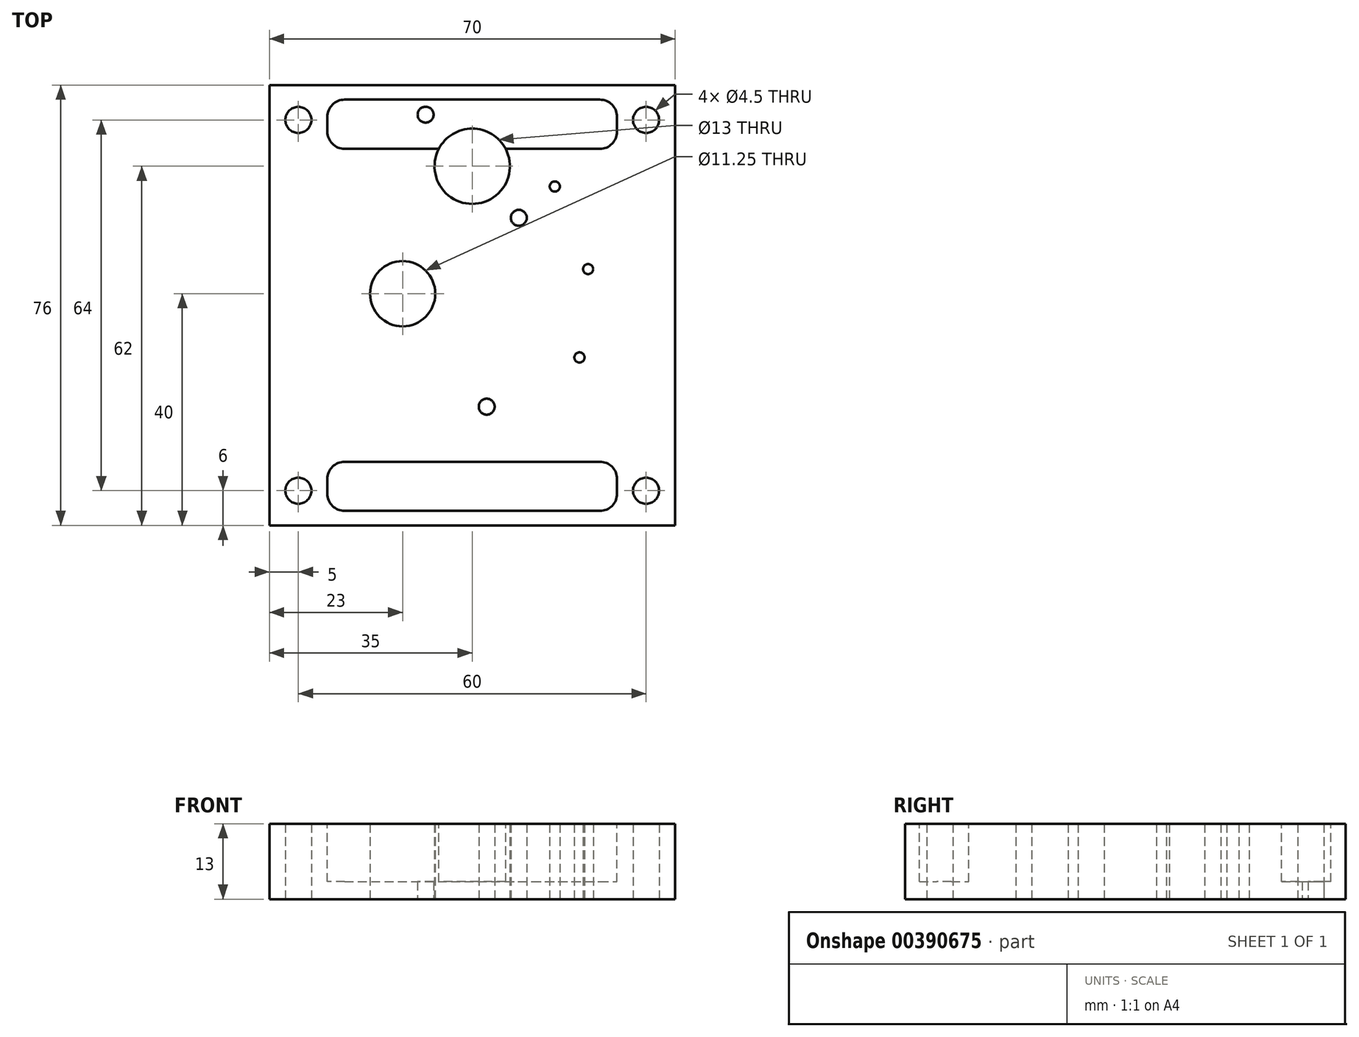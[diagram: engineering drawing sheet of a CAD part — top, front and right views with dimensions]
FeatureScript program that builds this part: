
annotation { "Feature Type Name" : "Feature", "Feature Type Description" : "" }
export const myFeature = defineFeature(function(context is Context, id is Id, definition is map)
    precondition{}
    {
        {
            var Q0;
            Q0=qCreatedBy(makeId("Top.planeOp"),FACE);
            var sketch = newSketch(context, id + "F0", { "sketchPlane" : qUnion([Q0])});
            skLineSegment(sketch, "E0.bottom", {"start": v(-35, 38) * mm, "end": v(35, 38) * mm});
            skLineSegment(sketch, "E0.top", {"start": v(-35, -38) * mm, "end": v(35, -38) * mm});
            skLineSegment(sketch, "E0.left", {"start": v(-35, 38) * mm, "end": v(-35, -38) * mm});
            skLineSegment(sketch, "E0.right", {"start": v(35, 38) * mm, "end": v(35, -38) * mm});
            skCircle(sketch, "E1", {"center": v(-30, 32) * mm, "radius": 2.25 * mm});
            skCircle(sketch, "E2.MirrorC", {"center": v(30, 32) * mm, "radius": 2.25 * mm});
            skCircle(sketch, "E3.MirrorC", {"center": v(-30, -32) * mm, "radius": 2.25 * mm});
            skCircle(sketch, "E4.MirrorC", {"center": v(30, -32) * mm, "radius": 2.25 * mm});
            skCircle(sketch, "E5", {"center": v(-12, 2) * mm, "radius": 5.62 * mm});
            skCircle(sketch, "E6", {"center": v(2.5, -17.5) * mm, "radius": 1.38 * mm});
            skCircle(sketch, "E7", {"center": v(18.5, -9) * mm, "radius": 0.88 * mm});
            skCircle(sketch, "E8", {"center": v(20, 6.25) * mm, "radius": 0.87 * mm});
            skCircle(sketch, "E9", {"center": v(14.25, 20.5) * mm, "radius": 0.87 * mm});
            skCircle(sketch, "E10", {"center": v(0, 24) * mm, "radius": 6.5 * mm});
            skCircle(sketch, "E11", {"center": v(-12, 2) * mm, "radius": 21 * mm, "construction": true});
            skCircle(sketch, "E12", {"center": v(14.25, 20.5) * mm, "radius": 5.5 * mm, "construction": true});
            skCircle(sketch, "E13", {"center": v(20, 6.25) * mm, "radius": 11 * mm, "construction": true});
            skLineSegment(sketch, "E14", {"start": v(8.04, 15.1) * mm, "end": v(0, 24) * mm, "construction": true});
            skLineSegment(sketch, "E15", {"start": v(0, 24) * mm, "end": v(-8.04, 32.9) * mm, "construction": true});
            skCircle(sketch, "E16", {"center": v(8.04, 15.1) * mm, "radius": 1.38 * mm});
            skCircle(sketch, "E17", {"center": v(-8.04, 32.9) * mm, "radius": 1.38 * mm});
            skSolve(sketch);
        }
        {
            var Q0;
            Q0=qSketchRegion(id+"F0",true);
            extrude(context, id + "F1", {"entities" : qUnion([Q0]), "depth" : 13 * mm, "offsetDistance" : 25 * mm});
        }
        {
            var Q0;
            Q0=makeQuery(id+"F1.opExtrude","CAP_FACE",FACE,{"disambiguationData":[OSD([sQuery(id+"F0.wireOp",EDGE,"E0.bottom"),sQuery(id+"F0.wireOp",EDGE,"E0.top"),sQuery(id+"F0.wireOp",EDGE,"E0.left"),sQuery(id+"F0.wireOp",EDGE,"E0.right"),sQuery(id+"F0.wireOp",EDGE,"E1"),sQuery(id+"F0.wireOp",EDGE,"E2.MirrorC"),sQuery(id+"F0.wireOp",EDGE,"E3.MirrorC"),sQuery(id+"F0.wireOp",EDGE,"E4.MirrorC")])],"isStart":false});
            var sketch = newSketch(context, id + "F2", { "sketchPlane" : qUnion([Q0])});
            skLineSegment(sketch, "E18.bottom", {"start": v(-32.5, 27) * mm, "end": v(32.5, 27) * mm});
            skLineSegment(sketch, "E18.top", {"start": v(-32.5, -27) * mm, "end": v(32.5, -27) * mm});
            skLineSegment(sketch, "E18.left", {"start": v(-32.5, 27) * mm, "end": v(-32.5, -27) * mm});
            skLineSegment(sketch, "E18.right", {"start": v(32.5, 27) * mm, "end": v(32.5, -27) * mm});
            skLineSegment(sketch, "E19.bottom", {"start": v(-25, 27) * mm, "end": v(25, 27) * mm});
            skLineSegment(sketch, "E19.top", {"start": v(-25, 35.5) * mm, "end": v(25, 35.5) * mm});
            skLineSegment(sketch, "E19.left", {"start": v(-25, 27) * mm, "end": v(-25, 35.5) * mm});
            skLineSegment(sketch, "E19.right", {"start": v(25, 27) * mm, "end": v(25, 35.5) * mm});
            skLineSegment(sketch, "E20.MirrorCS", {"start": v(-25, -27) * mm, "end": v(-25, -35.5) * mm});
            skLineSegment(sketch, "E21.MirrorCS", {"start": v(-25, -35.5) * mm, "end": v(25, -35.5) * mm});
            skLineSegment(sketch, "E22.MirrorCS", {"start": v(25, -27) * mm, "end": v(25, -35.5) * mm});
            skSolve(sketch);
        }
        {
            var Q0;
            {var subQ5=sQuery(id+"F2.wireOp",EDGE,"E18.left");Q0=makeQuery(id+"F2.imprint","IMPRINT",FACE,{"disambiguationData":[TD([[makeQuery(id+"F2.imprint","IMPRINT",EDGE,{"derivedFrom":subQ5}),1.0]])]});}
            var Q1;
            Q1=makeQuery(id+"F2.imprint","IMPRINT",FACE,{"disambiguationData":[TD([[makeQuery(id+"F2.imprint","IMPRINT",EDGE,{"derivedFrom":sQuery(id+"F2.wireOp",EDGE,"E19.top")}),-1.0]])]});
            var Q2;
            {var subQ0=sQuery(id+"F2.wireOp",EDGE,"E20.MirrorCS");Q2=makeQuery(id+"F2.imprint","IMPRINT",FACE,{"disambiguationData":[TD([[makeQuery(id+"F2.imprint","IMPRINT",EDGE,{"derivedFrom":subQ0}),1.0]])]});}
            extrude(context, id + "F3", {"entities" : qUnion([Q0, Q1, Q2]), "operationType" : NewBodyOperationType.REMOVE, "oppositeDirection" : true, "depth" : 10 * mm, "offsetDistance" : 25 * mm});
        }
        {
            var Q0;
            Q0=makeQuery(id+"F3.boolean.opBoolean","COPY",EDGE,{"derivedFrom":makeQuery(id+"F3.opExtrude","SWEPT_EDGE",EDGE,{"disambiguationData":[OSD([sQuery(id+"F2.wireOp",EDGE,"E18.bottom"),sQuery(id+"F2.wireOp",EDGE,"E19.left")])]})});
            var Q1;
            Q1=makeQuery(id+"F3.boolean.opBoolean","COPY",EDGE,{"derivedFrom":makeQuery(id+"F3.opExtrude","SWEPT_EDGE",EDGE,{"disambiguationData":[OSD([sQuery(id+"F2.wireOp",EDGE,"E18.bottom"),sQuery(id+"F2.wireOp",EDGE,"E19.right")])]})});
            var Q2;
            Q2=makeQuery(id+"F3.boolean.opBoolean","COPY",EDGE,{"derivedFrom":makeQuery(id+"F3.opExtrude","SWEPT_EDGE",EDGE,{"disambiguationData":[OSD([sQuery(id+"F2.wireOp",EDGE,"E18.top"),sQuery(id+"F2.wireOp",EDGE,"E20.MirrorCS")])]})});
            var Q3;
            Q3=makeQuery(id+"F3.boolean.opBoolean","COPY",EDGE,{"derivedFrom":makeQuery(id+"F3.opExtrude","SWEPT_EDGE",EDGE,{"disambiguationData":[OSD([sQuery(id+"F2.wireOp",EDGE,"E18.top"),sQuery(id+"F2.wireOp",EDGE,"E22.MirrorCS")])]})});
            var Q4;
            Q4=makeQuery(id+"F3.boolean.opBoolean","COPY",EDGE,{"derivedFrom":makeQuery(id+"F3.opExtrude","SWEPT_EDGE",EDGE,{"disambiguationData":[OSD([sQuery(id+"F2.wireOp",EDGE,"E18.top"),sQuery(id+"F2.wireOp",EDGE,"E18.right")])]})});
            var Q5;
            Q5=makeQuery(id+"F3.boolean.opBoolean","COPY",EDGE,{"derivedFrom":makeQuery(id+"F3.opExtrude","SWEPT_EDGE",EDGE,{"disambiguationData":[OSD([sQuery(id+"F2.wireOp",EDGE,"E18.bottom"),sQuery(id+"F2.wireOp",EDGE,"E18.right")])]})});
            var Q6;
            Q6=makeQuery(id+"F3.boolean.opBoolean","COPY",EDGE,{"derivedFrom":makeQuery(id+"F3.opExtrude","SWEPT_EDGE",EDGE,{"disambiguationData":[OSD([sQuery(id+"F2.wireOp",EDGE,"E19.top"),sQuery(id+"F2.wireOp",EDGE,"E19.right")])]})});
            var Q7;
            Q7=makeQuery(id+"F3.boolean.opBoolean","COPY",EDGE,{"derivedFrom":makeQuery(id+"F3.opExtrude","SWEPT_EDGE",EDGE,{"disambiguationData":[OSD([sQuery(id+"F2.wireOp",EDGE,"E19.top"),sQuery(id+"F2.wireOp",EDGE,"E19.left")])]})});
            var Q8;
            Q8=makeQuery(id+"F3.boolean.opBoolean","COPY",EDGE,{"derivedFrom":makeQuery(id+"F3.opExtrude","SWEPT_EDGE",EDGE,{"disambiguationData":[OSD([sQuery(id+"F2.wireOp",EDGE,"E18.bottom"),sQuery(id+"F2.wireOp",EDGE,"E18.left")])]})});
            var Q9;
            Q9=makeQuery(id+"F3.boolean.opBoolean","COPY",EDGE,{"derivedFrom":makeQuery(id+"F3.opExtrude","SWEPT_EDGE",EDGE,{"disambiguationData":[OSD([sQuery(id+"F2.wireOp",EDGE,"E18.top"),sQuery(id+"F2.wireOp",EDGE,"E18.left")])]})});
            var Q10;
            Q10=makeQuery(id+"F3.boolean.opBoolean","COPY",EDGE,{"derivedFrom":makeQuery(id+"F3.opExtrude","SWEPT_EDGE",EDGE,{"disambiguationData":[OSD([sQuery(id+"F2.wireOp",EDGE,"E20.MirrorCS"),sQuery(id+"F2.wireOp",EDGE,"E21.MirrorCS")])]})});
            var Q11;
            Q11=makeQuery(id+"F3.boolean.opBoolean","COPY",EDGE,{"derivedFrom":makeQuery(id+"F3.opExtrude","SWEPT_EDGE",EDGE,{"disambiguationData":[OSD([sQuery(id+"F2.wireOp",EDGE,"E21.MirrorCS"),sQuery(id+"F2.wireOp",EDGE,"E22.MirrorCS")])]})});
            fillet(context, id + "F4", {"entities" : qUnion([Q0, Q1, Q2, Q3, Q4, Q5, Q6, Q7, Q8, Q9, Q10, Q11]), "radius" : 3 * mm, "tangentPropagation" : true, "allowEdgeOverflow" : false});
        }
    });
